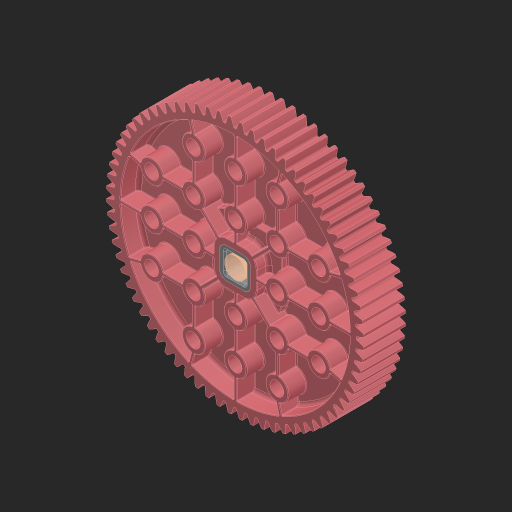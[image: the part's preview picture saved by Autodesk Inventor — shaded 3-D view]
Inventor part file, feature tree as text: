
AUTODESK INVENTOR PART (.ipt)
format: ipt  version: 2023 (Build 270158000, 158)  size: 4,226,048 bytes
history: native  units: in
note: dims shown in document units (in); Inventor stores cm internally (conversion verified against a paired STEP export)
features: other x3, sketch x1, extrude x1
ambient origin geometry x8: Origin, YZ Plane, XZ Plane, XY Plane, X Axis, Y Axis, Z Axis, Center Point
bodies: Solid1 (feature_tree), Solid2 (feature_tree)
feature tree (5):
  sketch  "Sketch1"  dims[d0=0.25in d1=0.3937in d2=0.0in]
  other  "Srf1"
  other  "276-7574-001_OVERMOLD Rev4_72T 24DP Gear_1:1"
  other  "276-7573-002 Rev7_2:1"
  extrude  "ExtrusionSrf1"  Depth=0.3937in TaperAngle=0.0deg
